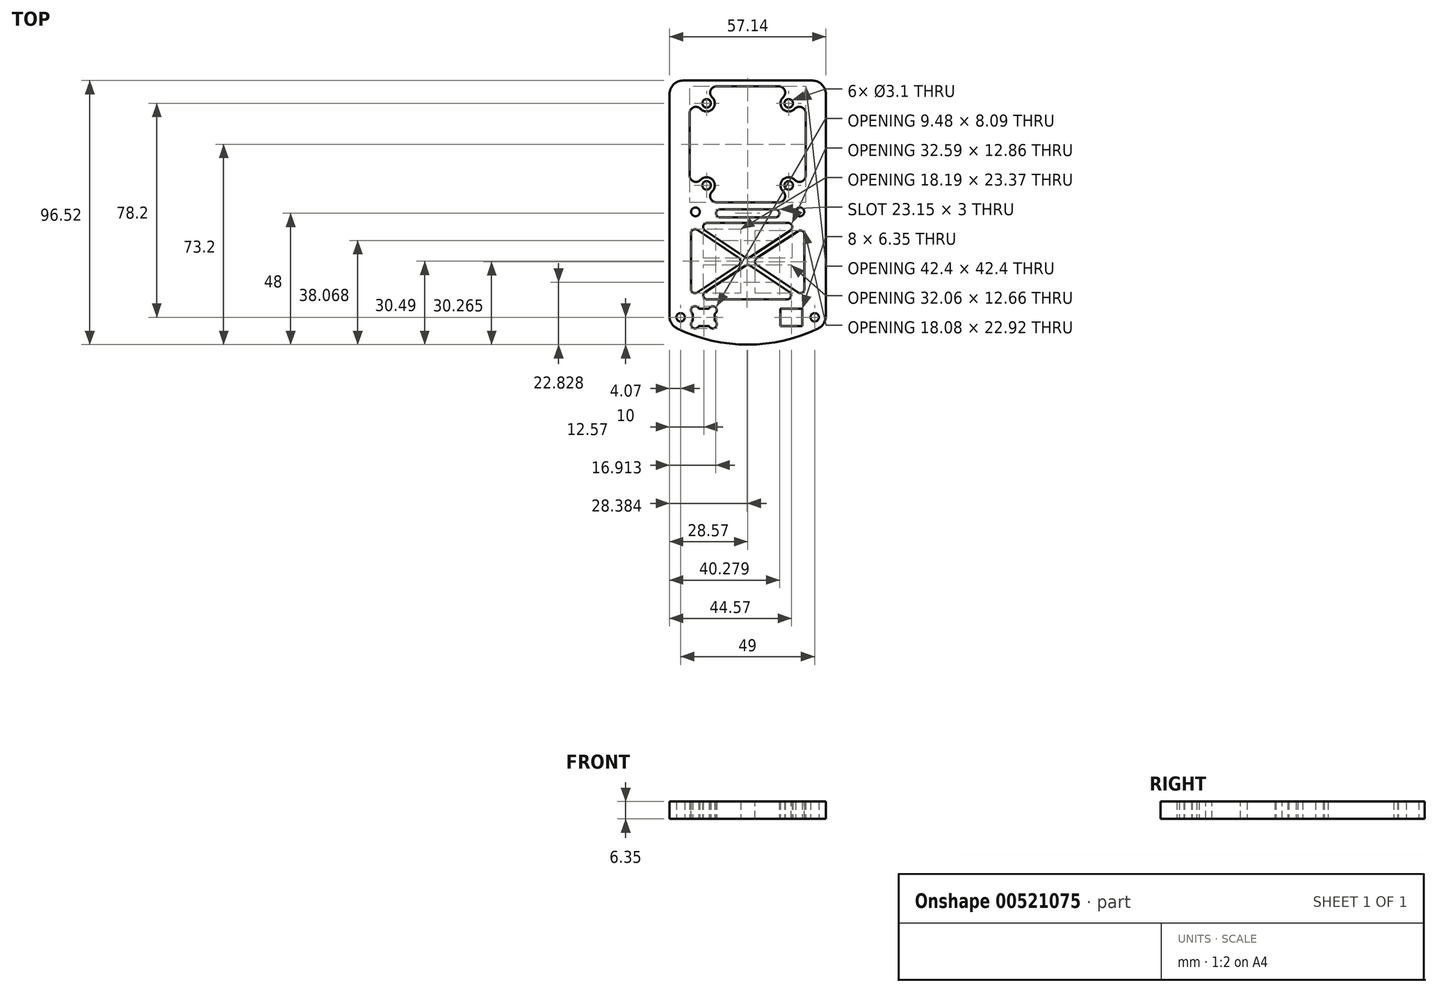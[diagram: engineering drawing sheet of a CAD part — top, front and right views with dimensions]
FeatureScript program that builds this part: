
annotation { "Feature Type Name" : "Feature", "Feature Type Description" : "" }
export const myFeature = defineFeature(function(context is Context, id is Id, definition is map)
    precondition{}
    {
        {
            var Q0;
            Q0=qCreatedBy(makeId("Top.planeOp"),FACE);
            var sketch = newSketch(context, id + "F0", { "sketchPlane" : qUnion([Q0])});
            skLineSegment(sketch, "E0.bottom", {"start": v(23.58, 47.02) * mm, "end": v(-23.58, 47.02) * mm});
            skLineSegment(sketch, "E0.top", {"start": v(23.58, -49.5) * mm, "end": v(-23.58, -49.5) * mm, "construction": true});
            skLineSegment(sketch, "E0.left", {"start": v(28.57, 42.02) * mm, "end": v(28.57, -39.08) * mm});
            skLineSegment(sketch, "E0.right", {"start": v(-28.58, 42.02) * mm, "end": v(-28.58, -39.08) * mm});
            skPoint(sketch, "E0.middle", {"position": v(0, 0) * mm});
            skCircle(sketch, "E1", {"center": v(-24.5, -39.5) * mm, "radius": 1.55 * mm});
            skLineSegment(sketch, "E2", {"start": v(0, 44.9) * mm, "end": v(11.41, 44.9) * mm});
            skLineSegment(sketch, "E3", {"start": v(21.2, 35.11) * mm, "end": v(21.2, 23.7) * mm});
            skLineSegment(sketch, "E4", {"start": v(36.97, 23.7) * mm, "end": v(-37.23, 23.7) * mm, "construction": true});
            skCircle(sketch, "E5", {"center": v(-19.08, -0.98) * mm, "radius": 1.6 * mm});
            skLineSegment(sketch, "E6.MirrorCS", {"start": v(0, 44.9) * mm, "end": v(-11.41, 44.9) * mm});
            skLineSegment(sketch, "E7.MirrorCS", {"start": v(-21.2, 35.11) * mm, "end": v(-21.2, 23.7) * mm});
            skLineSegment(sketch, "E8.MirrorCS", {"start": v(21.2, 12.29) * mm, "end": v(21.2, 23.7) * mm});
            skLineSegment(sketch, "E9.MirrorCS", {"start": v(0, 2.5) * mm, "end": v(11.41, 2.5) * mm});
            skLineSegment(sketch, "E10.MirrorCS", {"start": v(0, 2.5) * mm, "end": v(-11.41, 2.5) * mm});
            skLineSegment(sketch, "E11.MirrorCS", {"start": v(-21.2, 12.29) * mm, "end": v(-21.2, 23.7) * mm});
            skPoint(sketch, "E12.MirrorP", {"position": v(0, 47.4) * mm});
            skPoint(sketch, "E13.visualSharp", {"position": v(-28.58, 47.02) * mm});
            skArc(sketch, "E13.filletArc", {"start": v(-23.58, 47.02) * mm, "mid": v(-27.11, 45.56) * mm, "end": v(-28.58, 42.02) * mm});
            skPoint(sketch, "E14.visualSharp", {"position": v(28.57, 47.02) * mm});
            skArc(sketch, "E14.filletArc", {"start": v(28.58, 42.02) * mm, "mid": v(27.11, 45.56) * mm, "end": v(23.58, 47.02) * mm});
            skCircle(sketch, "E15", {"center": v(-15, 8.7) * mm, "radius": 1.55 * mm});
            skCircle(sketch, "E16.MirrorC", {"center": v(15, 8.7) * mm, "radius": 1.55 * mm});
            skCircle(sketch, "E17.MirrorC", {"center": v(15, 38.7) * mm, "radius": 1.55 * mm});
            skCircle(sketch, "E18.MirrorC", {"center": v(-15, 38.7) * mm, "radius": 1.55 * mm});
            skCircle(sketch, "E19.MirrorC", {"center": v(19.08, -0.98) * mm, "radius": 1.6 * mm});
            skArc(sketch, "E20", {"start": v(10.07, -3) * mm, "mid": v(11.57, -1.5) * mm, "end": v(10.07, 0) * mm});
            skArc(sketch, "E21", {"start": v(-11.41, 2.5) * mm, "mid": v(-13.55, 3.96) * mm, "end": v(-12.97, 6.5) * mm});
            skArc(sketch, "E22", {"start": v(-17.2, 10.73) * mm, "mid": v(-19.74, 10.15) * mm, "end": v(-21.2, 12.29) * mm});
            skArc(sketch, "E23.MirrorCS", {"start": v(11.41, 2.5) * mm, "mid": v(13.55, 3.96) * mm, "end": v(12.97, 6.5) * mm});
            skArc(sketch, "E24.MirrorCS", {"start": v(17.2, 10.73) * mm, "mid": v(19.74, 10.15) * mm, "end": v(21.2, 12.29) * mm});
            skArc(sketch, "E25.MirrorCS", {"start": v(-17.2, 36.67) * mm, "mid": v(-19.74, 37.25) * mm, "end": v(-21.2, 35.11) * mm});
            skArc(sketch, "E26.MirrorCS", {"start": v(-11.41, 44.9) * mm, "mid": v(-13.55, 43.44) * mm, "end": v(-12.97, 40.9) * mm});
            skArc(sketch, "E27.MirrorCS", {"start": v(17.2, 36.67) * mm, "mid": v(19.74, 37.25) * mm, "end": v(21.2, 35.11) * mm});
            skArc(sketch, "E28.MirrorCS", {"start": v(11.41, 44.9) * mm, "mid": v(13.55, 43.44) * mm, "end": v(12.97, 40.9) * mm});
            skLineSegment(sketch, "E29.bottom", {"start": v(10.08, 0) * mm, "end": v(0, 0) * mm});
            skLineSegment(sketch, "E29.top", {"start": v(10.07, -3) * mm, "end": v(0, -3) * mm});
            skLineSegment(sketch, "E29.right", {"start": v(0, 0) * mm, "end": v(0, -3) * mm});
            skLineSegment(sketch, "E30.MirrorCS", {"start": v(-10.07, -3) * mm, "end": v(0, -3) * mm});
            skArc(sketch, "E31.MirrorC", {"start": v(-10.07, -3) * mm, "mid": v(-11.57, -1.5) * mm, "end": v(-10.08, 0) * mm});
            skLineSegment(sketch, "E32.MirrorCS", {"start": v(-10.08, 0) * mm, "end": v(0, 0) * mm});
            skLineSegment(sketch, "E33", {"start": v(10.08, 0) * mm, "end": v(10.08, -3) * mm, "construction": true});
            skLineSegment(sketch, "E34", {"start": v(-10.08, 0) * mm, "end": v(-10.08, -3) * mm, "construction": true});
            skLineSegment(sketch, "E35", {"start": v(0, 23.7) * mm, "end": v(-36.43, -12.73) * mm, "construction": true});
            skPoint(sketch, "E36.orphan", {"position": v(0, 57.71) * mm});
            skArc(sketch, "E37", {"start": v(-12.97, 6.5) * mm, "mid": v(-12.88, 10.82) * mm, "end": v(-17.2, 10.73) * mm});
            skArc(sketch, "E38.MirrorCS", {"start": v(12.97, 6.5) * mm, "mid": v(12.88, 10.82) * mm, "end": v(17.2, 10.73) * mm});
            skArc(sketch, "E39.MirrorCS", {"start": v(-12.97, 40.9) * mm, "mid": v(-12.88, 36.58) * mm, "end": v(-17.2, 36.67) * mm});
            skArc(sketch, "E40.MirrorCS", {"start": v(12.97, 40.9) * mm, "mid": v(12.88, 36.58) * mm, "end": v(17.2, 36.67) * mm});
            skLineSegment(sketch, "E41", {"start": v(-24.5, -39.5) * mm, "end": v(24.5, -39.5) * mm, "construction": true});
            skLineSegment(sketch, "E42.bottom", {"start": v(-12, -36.33) * mm, "end": v(-20, -36.33) * mm});
            skLineSegment(sketch, "E42.top", {"start": v(-12, -42.68) * mm, "end": v(-20, -42.68) * mm});
            skLineSegment(sketch, "E42.left", {"start": v(-12, -36.33) * mm, "end": v(-12, -42.68) * mm});
            skLineSegment(sketch, "E42.right", {"start": v(-20, -36.33) * mm, "end": v(-20, -42.68) * mm});
            skPoint(sketch, "E42.middle", {"position": v(-16, -39.5) * mm});
            skLineSegment(sketch, "E43", {"start": v(0, 67.13) * mm, "end": v(0, -67.36) * mm, "construction": true});
            skPoint(sketch, "E43.endSnap0", {"position": v(0, -49.5) * mm});
            skLineSegment(sketch, "E44.MirrorCS", {"start": v(12, -36.33) * mm, "end": v(12, -42.68) * mm});
            skLineSegment(sketch, "E45.MirrorCS", {"start": v(12, -42.68) * mm, "end": v(20, -42.68) * mm});
            skLineSegment(sketch, "E46.MirrorCS", {"start": v(20, -36.33) * mm, "end": v(20, -42.68) * mm});
            skLineSegment(sketch, "E47.MirrorCS", {"start": v(12, -36.33) * mm, "end": v(20, -36.33) * mm});
            skCircle(sketch, "E48.MirrorC", {"center": v(24.5, -39.5) * mm, "radius": 1.55 * mm});
            skArc(sketch, "E49", {"start": v(-28.58, -39.08) * mm, "mid": v(-27.81, -41.74) * mm, "end": v(-25.76, -43.58) * mm});
            skArc(sketch, "E50", {"start": v(28.58, -39.08) * mm, "mid": v(27.81, -41.74) * mm, "end": v(25.76, -43.58) * mm});
            skArc(sketch, "E51", {"start": v(-25.76, -43.58) * mm, "mid": v(0, -49.5) * mm, "end": v(25.76, -43.58) * mm});
            skSolve(sketch);
        }
        {
            var Q0;
            Q0 = qSketchRegion(id + "F0", true);
            extrude(context, id + "F1", {"entities" : qUnion([Q0]), "depth" : 6.35 * mm, "offsetDistance" : 25 * mm});
        }
        {
            var Q0;
            Q0=makeQuery(id+"F1.opExtrude","CAP_FACE",FACE,{"disambiguationData":[OSD([sQuery(id+"F0.wireOp",EDGE,"E0.bottom"),sQuery(id+"F0.wireOp",EDGE,"E0.left"),sQuery(id+"F0.wireOp",EDGE,"E0.right"),sQuery(id+"F0.wireOp",EDGE,"E1"),sQuery(id+"F0.wireOp",EDGE,"E3"),sQuery(id+"F0.wireOp",EDGE,"E5"),sQuery(id+"F0.wireOp",EDGE,"E7.MirrorCS"),sQuery(id+"F0.wireOp",EDGE,"E8.MirrorCS"),sQuery(id+"F0.wireOp",EDGE,"E9.MirrorCS"),sQuery(id+"F0.wireOp",EDGE,"E10.MirrorCS"),sQuery(id+"F0.wireOp",EDGE,"E11.MirrorCS"),sQuery(id+"F0.wireOp",EDGE,"E13.filletArc"),sQuery(id+"F0.wireOp",EDGE,"E14.filletArc"),sQuery(id+"F0.wireOp",EDGE,"E16.MirrorC"),sQuery(id+"F0.wireOp",EDGE,"E15"),sQuery(id+"F0.wireOp",EDGE,"E17.MirrorC"),sQuery(id+"F0.wireOp",EDGE,"E18.MirrorC"),sQuery(id+"F0.wireOp",EDGE,"E19.MirrorC"),sQuery(id+"F0.wireOp",EDGE,"E20"),sQuery(id+"F0.wireOp",EDGE,"E21"),sQuery(id+"F0.wireOp",EDGE,"E22"),sQuery(id+"F0.wireOp",EDGE,"E23.MirrorCS"),sQuery(id+"F0.wireOp",EDGE,"E24.MirrorCS"),sQuery(id+"F0.wireOp",EDGE,"E2"),sQuery(id+"F0.wireOp",EDGE,"E6.MirrorCS"),sQuery(id+"F0.wireOp",EDGE,"E25.MirrorCS"),sQuery(id+"F0.wireOp",EDGE,"E26.MirrorCS"),sQuery(id+"F0.wireOp",EDGE,"E27.MirrorCS"),sQuery(id+"F0.wireOp",EDGE,"E28.MirrorCS"),sQuery(id+"F0.wireOp",EDGE,"E29.right"),sQuery(id+"F0.wireOp",EDGE,"E30.MirrorCS"),sQuery(id+"F0.wireOp",EDGE,"E31.MirrorC"),sQuery(id+"F0.wireOp",EDGE,"E32.MirrorCS"),sQuery(id+"F0.wireOp",EDGE,"E37"),sQuery(id+"F0.wireOp",EDGE,"E38.MirrorCS"),sQuery(id+"F0.wireOp",EDGE,"E39.MirrorCS"),sQuery(id+"F0.wireOp",EDGE,"E40.MirrorCS"),sQuery(id+"F0.wireOp",EDGE,"E42.bottom"),sQuery(id+"F0.wireOp",EDGE,"E42.top"),sQuery(id+"F0.wireOp",EDGE,"E42.left"),sQuery(id+"F0.wireOp",EDGE,"E42.right"),sQuery(id+"F0.wireOp",EDGE,"E44.MirrorCS"),sQuery(id+"F0.wireOp",EDGE,"E45.MirrorCS"),sQuery(id+"F0.wireOp",EDGE,"E46.MirrorCS"),sQuery(id+"F0.wireOp",EDGE,"E47.MirrorCS"),sQuery(id+"F0.wireOp",EDGE,"E48.MirrorC"),sQuery(id+"F0.wireOp",EDGE,"E49"),sQuery(id+"F0.wireOp",EDGE,"E50"),sQuery(id+"F0.wireOp",EDGE,"E51")])],"isStart":false});
            var sketch = newSketch(context, id + "F2", { "sketchPlane" : qUnion([Q0])});
            skLineSegment(sketch, "E52.bottom", {"start": v(20.75, -5) * mm, "end": v(-20.75, -5) * mm});
            skLineSegment(sketch, "E52.top", {"start": v(20.75, -33) * mm, "end": v(-20.75, -33) * mm});
            skLineSegment(sketch, "E52.left", {"start": v(20.75, -5) * mm, "end": v(20.75, -33) * mm});
            skLineSegment(sketch, "E52.right", {"start": v(-20.75, -5) * mm, "end": v(-20.75, -33) * mm});
            skPoint(sketch, "E52.middle", {"position": v(0, -19) * mm});
            skLineSegment(sketch, "E53", {"start": v(-19.75, -5) * mm, "end": v(19.75, -5) * mm, "construction": true});
            skLineSegment(sketch, "E54", {"start": v(20.75, -6.5) * mm, "end": v(20.75, -32) * mm, "construction": true});
            skLineSegment(sketch, "E55", {"start": v(19.25, -33) * mm, "end": v(-19.75, -33) * mm, "construction": true});
            skLineSegment(sketch, "E56", {"start": v(-20.75, -6) * mm, "end": v(-20.75, -32) * mm, "construction": true});
            skLineSegment(sketch, "E57", {"start": v(-19.75, -5) * mm, "end": v(20.75, -32) * mm});
            skLineSegment(sketch, "E58", {"start": v(19.25, -33) * mm, "end": v(-20.75, -6) * mm});
            skLineSegment(sketch, "E59", {"start": v(-20.75, -32) * mm, "end": v(19.75, -5) * mm});
            skLineSegment(sketch, "E60", {"start": v(-19.75, -33) * mm, "end": v(20.75, -6.5) * mm});
            skSolve(sketch);
        }
        {
            var Q0;
            {var subQ0=sQuery(id+"F2.wireOp",EDGE,"E58");var subQ1=sQuery(id+"F2.wireOp",EDGE,"E52.right");var subQ2=makeQuery(id+"F2.imprint","INTERSECT",VERTEX,{"derivedFrom":[subQ1,subQ0]});Q0=makeQuery(id+"F2.imprint","IMPRINT",FACE,{"disambiguationData":[TD([[makeQuery(id+"F2.imprint","IMPRINT",EDGE,{"disambiguationData":[TD([[subQ2,-1.0]])],"derivedFrom":subQ1}),1.0]])]});}
            var Q1;
            {var subQ0=sQuery(id+"F2.wireOp",EDGE,"E57");var subQ1=sQuery(id+"F2.wireOp",EDGE,"E52.bottom");var subQ2=makeQuery(id+"F2.imprint","INTERSECT",VERTEX,{"derivedFrom":[subQ1,subQ0]});Q1=makeQuery(id+"F2.imprint","IMPRINT",FACE,{"disambiguationData":[TD([[makeQuery(id+"F2.imprint","IMPRINT",EDGE,{"disambiguationData":[TD([[subQ2,1.0]])],"derivedFrom":subQ1}),1.0]])]});}
            var Q2;
            {var subQ0=sQuery(id+"F2.wireOp",EDGE,"E57");var subQ1=sQuery(id+"F2.wireOp",EDGE,"E52.left");var subQ2=makeQuery(id+"F2.imprint","INTERSECT",VERTEX,{"derivedFrom":[subQ1,subQ0]});Q2=makeQuery(id+"F2.imprint","IMPRINT",FACE,{"disambiguationData":[TD([[makeQuery(id+"F2.imprint","IMPRINT",EDGE,{"disambiguationData":[TD([[subQ2,1.0]])],"derivedFrom":subQ1}),-1.0]])]});}
            var Q3;
            {var subQ0=sQuery(id+"F2.wireOp",EDGE,"E58");var subQ1=sQuery(id+"F2.wireOp",EDGE,"E52.top");var subQ2=makeQuery(id+"F2.imprint","INTERSECT",VERTEX,{"derivedFrom":[subQ1,subQ0]});Q3=makeQuery(id+"F2.imprint","IMPRINT",FACE,{"disambiguationData":[TD([[makeQuery(id+"F2.imprint","IMPRINT",EDGE,{"disambiguationData":[TD([[subQ2,-1.0]])],"derivedFrom":subQ1}),-1.0]])]});}
            extrude(context, id + "F3", {"entities" : qUnion([Q0, Q1, Q2, Q3]), "operationType" : NewBodyOperationType.REMOVE, "oppositeDirection" : true, "depth" : 25 * mm, "offsetDistance" : 25 * mm});
        }
        {
            var Q0;
            Q0=makeQuery(id+"F3.boolean.opBoolean","COPY",EDGE,{"derivedFrom":makeQuery(id+"F3.opExtrude","SWEPT_EDGE",EDGE,{"disambiguationData":[OSD([sQuery(id+"F2.wireOp",EDGE,"E52.right"),sQuery(id+"F2.wireOp",EDGE,"E58")])]})});
            var Q1;
            Q1=makeQuery(id+"F3.boolean.opBoolean","COPY",EDGE,{"derivedFrom":makeQuery(id+"F3.opExtrude","SWEPT_EDGE",EDGE,{"disambiguationData":[OSD([sQuery(id+"F2.wireOp",EDGE,"E52.right"),sQuery(id+"F2.wireOp",EDGE,"E59")])]})});
            var Q2;
            Q2=makeQuery(id+"F3.boolean.opBoolean","COPY",EDGE,{"derivedFrom":makeQuery(id+"F3.opExtrude","SWEPT_EDGE",EDGE,{"disambiguationData":[OSD([sQuery(id+"F2.wireOp",EDGE,"E52.bottom"),sQuery(id+"F2.wireOp",EDGE,"E57")])]})});
            var Q3;
            Q3=makeQuery(id+"F3.boolean.opBoolean","COPY",EDGE,{"derivedFrom":makeQuery(id+"F3.opExtrude","SWEPT_EDGE",EDGE,{"disambiguationData":[OSD([sQuery(id+"F2.wireOp",EDGE,"E52.bottom"),sQuery(id+"F2.wireOp",EDGE,"E59")])]})});
            var Q4;
            Q4=makeQuery(id+"F3.boolean.opBoolean","COPY",EDGE,{"derivedFrom":makeQuery(id+"F3.opExtrude","SWEPT_EDGE",EDGE,{"disambiguationData":[OSD([sQuery(id+"F2.wireOp",EDGE,"E52.left"),sQuery(id+"F2.wireOp",EDGE,"E60")])]})});
            var Q5;
            Q5=makeQuery(id+"F3.boolean.opBoolean","COPY",EDGE,{"derivedFrom":makeQuery(id+"F3.opExtrude","SWEPT_EDGE",EDGE,{"disambiguationData":[OSD([sQuery(id+"F2.wireOp",EDGE,"E52.left"),sQuery(id+"F2.wireOp",EDGE,"E57")])]})});
            var Q6;
            Q6=makeQuery(id+"F3.boolean.opBoolean","COPY",EDGE,{"derivedFrom":makeQuery(id+"F3.opExtrude","SWEPT_EDGE",EDGE,{"disambiguationData":[OSD([sQuery(id+"F2.wireOp",EDGE,"E52.top"),sQuery(id+"F2.wireOp",EDGE,"E58")])]})});
            var Q7;
            Q7=makeQuery(id+"F3.boolean.opBoolean","COPY",EDGE,{"derivedFrom":makeQuery(id+"F3.opExtrude","SWEPT_EDGE",EDGE,{"disambiguationData":[OSD([sQuery(id+"F2.wireOp",EDGE,"E52.top"),sQuery(id+"F2.wireOp",EDGE,"E60")])]})});
            var Q8;
            Q8=makeQuery(id+"F3.boolean.opBoolean","COPY",EDGE,{"derivedFrom":makeQuery(id+"F3.opExtrude","SWEPT_EDGE",EDGE,{"disambiguationData":[OSD([sQuery(id+"F2.wireOp",EDGE,"E58"),sQuery(id+"F2.wireOp",EDGE,"E60")])]})});
            var Q9;
            Q9=makeQuery(id+"F3.boolean.opBoolean","COPY",EDGE,{"derivedFrom":makeQuery(id+"F3.opExtrude","SWEPT_EDGE",EDGE,{"disambiguationData":[OSD([sQuery(id+"F2.wireOp",EDGE,"E57"),sQuery(id+"F2.wireOp",EDGE,"E60")])]})});
            var Q10;
            Q10=makeQuery(id+"F3.boolean.opBoolean","COPY",EDGE,{"derivedFrom":makeQuery(id+"F3.opExtrude","SWEPT_EDGE",EDGE,{"disambiguationData":[OSD([sQuery(id+"F2.wireOp",EDGE,"E57"),sQuery(id+"F2.wireOp",EDGE,"E59")])]})});
            var Q11;
            Q11=makeQuery(id+"F3.boolean.opBoolean","COPY",EDGE,{"derivedFrom":makeQuery(id+"F3.opExtrude","SWEPT_EDGE",EDGE,{"disambiguationData":[OSD([sQuery(id+"F2.wireOp",EDGE,"E58"),sQuery(id+"F2.wireOp",EDGE,"E59")])]})});
            fillet(context, id + "F4", {"entities" : qUnion([Q0, Q1, Q2, Q3, Q4, Q5, Q6, Q7, Q8, Q9, Q10, Q11]), "radius" : 1.5 * mm, "tangentPropagation" : true, "allowEdgeOverflow" : false});
        }
        {
            var Q0;
            Q0=makeQuery(id+"F1.opExtrude","CAP_FACE",FACE,{"disambiguationData":[OSD([sQuery(id+"F0.wireOp",EDGE,"E0.bottom"),sQuery(id+"F0.wireOp",EDGE,"E0.left"),sQuery(id+"F0.wireOp",EDGE,"E0.right"),sQuery(id+"F0.wireOp",EDGE,"E1"),sQuery(id+"F0.wireOp",EDGE,"E3"),sQuery(id+"F0.wireOp",EDGE,"E5"),sQuery(id+"F0.wireOp",EDGE,"E7.MirrorCS"),sQuery(id+"F0.wireOp",EDGE,"E8.MirrorCS"),sQuery(id+"F0.wireOp",EDGE,"E9.MirrorCS"),sQuery(id+"F0.wireOp",EDGE,"E10.MirrorCS"),sQuery(id+"F0.wireOp",EDGE,"E11.MirrorCS"),sQuery(id+"F0.wireOp",EDGE,"E13.filletArc"),sQuery(id+"F0.wireOp",EDGE,"E14.filletArc"),sQuery(id+"F0.wireOp",EDGE,"E16.MirrorC"),sQuery(id+"F0.wireOp",EDGE,"E15"),sQuery(id+"F0.wireOp",EDGE,"E17.MirrorC"),sQuery(id+"F0.wireOp",EDGE,"E18.MirrorC"),sQuery(id+"F0.wireOp",EDGE,"E19.MirrorC"),sQuery(id+"F0.wireOp",EDGE,"E20"),sQuery(id+"F0.wireOp",EDGE,"E21"),sQuery(id+"F0.wireOp",EDGE,"E22"),sQuery(id+"F0.wireOp",EDGE,"E23.MirrorCS"),sQuery(id+"F0.wireOp",EDGE,"E24.MirrorCS"),sQuery(id+"F0.wireOp",EDGE,"E2"),sQuery(id+"F0.wireOp",EDGE,"E6.MirrorCS"),sQuery(id+"F0.wireOp",EDGE,"E25.MirrorCS"),sQuery(id+"F0.wireOp",EDGE,"E26.MirrorCS"),sQuery(id+"F0.wireOp",EDGE,"E27.MirrorCS"),sQuery(id+"F0.wireOp",EDGE,"E28.MirrorCS"),sQuery(id+"F0.wireOp",EDGE,"E29.bottom"),sQuery(id+"F0.wireOp",EDGE,"E29.top"),sQuery(id+"F0.wireOp",EDGE,"E30.MirrorCS"),sQuery(id+"F0.wireOp",EDGE,"E31.MirrorC"),sQuery(id+"F0.wireOp",EDGE,"E32.MirrorCS"),sQuery(id+"F0.wireOp",EDGE,"E37"),sQuery(id+"F0.wireOp",EDGE,"E38.MirrorCS"),sQuery(id+"F0.wireOp",EDGE,"E39.MirrorCS"),sQuery(id+"F0.wireOp",EDGE,"E40.MirrorCS"),sQuery(id+"F0.wireOp",EDGE,"E42.bottom"),sQuery(id+"F0.wireOp",EDGE,"E42.top"),sQuery(id+"F0.wireOp",EDGE,"E42.left"),sQuery(id+"F0.wireOp",EDGE,"E42.right"),sQuery(id+"F0.wireOp",EDGE,"E44.MirrorCS"),sQuery(id+"F0.wireOp",EDGE,"E45.MirrorCS"),sQuery(id+"F0.wireOp",EDGE,"E46.MirrorCS"),sQuery(id+"F0.wireOp",EDGE,"E47.MirrorCS"),sQuery(id+"F0.wireOp",EDGE,"E48.MirrorC"),sQuery(id+"F0.wireOp",EDGE,"E49"),sQuery(id+"F0.wireOp",EDGE,"E50"),sQuery(id+"F0.wireOp",EDGE,"E51")])],"isStart":true});
            var sketch = newSketch(context, id + "F5", { "sketchPlane" : qUnion([Q0])});
            skLineSegment(sketch, "E61", {"start": v(-12, 36.33) * mm, "end": v(-20, 42.68) * mm, "construction": true});
            skLineSegment(sketch, "E62", {"start": v(-12, 42.68) * mm, "end": v(-20, 36.33) * mm, "construction": true});
            skLineSegment(sketch, "E63.bottom", {"start": v(-19.25, 36.92) * mm, "end": v(-12.75, 36.92) * mm, "construction": true});
            skLineSegment(sketch, "E63.top", {"start": v(-19.25, 42.08) * mm, "end": v(-12.75, 42.08) * mm, "construction": true});
            skLineSegment(sketch, "E63.left", {"start": v(-19.25, 36.92) * mm, "end": v(-19.25, 42.08) * mm, "construction": true});
            skLineSegment(sketch, "E63.right", {"start": v(-12.75, 36.92) * mm, "end": v(-12.75, 42.08) * mm, "construction": true});
            skPoint(sketch, "E63.middle", {"position": v(-16, 39.5) * mm});
            skCircle(sketch, "E64", {"center": v(-19.25, 36.92) * mm, "radius": 1.5 * mm});
            skCircle(sketch, "E65", {"center": v(-19.25, 42.08) * mm, "radius": 1.5 * mm});
            skCircle(sketch, "E66", {"center": v(-12.75, 42.08) * mm, "radius": 1.5 * mm});
            skCircle(sketch, "E67", {"center": v(-12.75, 36.92) * mm, "radius": 1.5 * mm});
            skLineSegment(sketch, "E68", {"start": v(0, 25.02) * mm, "end": v(0, 58.55) * mm, "construction": true});
            skCircle(sketch, "E69.MirrorC", {"center": v(12.75, 36.92) * mm, "radius": 1.5 * mm});
            skCircle(sketch, "E70.MirrorC", {"center": v(12.75, 42.08) * mm, "radius": 1.5 * mm});
            skCircle(sketch, "E71.MirrorC", {"center": v(19.25, 42.08) * mm, "radius": 1.5 * mm});
            skCircle(sketch, "E72.MirrorC", {"center": v(19.25, 36.92) * mm, "radius": 1.5 * mm});
            skSolve(sketch);
        }
        {
            var Q0;
            {var subQ0=sQuery(id+"F5.wireOp",EDGE,"E67");var subQ1=makeQuery(id+"F1.opExtrude","CAP_EDGE",EDGE,{"disambiguationData":[OSD([sQuery(id+"F0.wireOp",EDGE,"E42.bottom")])],"isStart":true});var subQ2=makeQuery(id+"F5.imprint","INTERSECT",VERTEX,{"derivedFrom":[subQ1,subQ0]});Q0=makeQuery(id+"F5.imprint","IMPRINT",FACE,{"disambiguationData":[TD([[makeQuery(id+"F5.imprint","IMPRINT",EDGE,{"disambiguationData":[TD([[subQ2,-1.0]])],"derivedFrom":subQ0}),1.0]])]});}
            var Q1;
            {var subQ0=sQuery(id+"F5.wireOp",EDGE,"E66");var subQ1=makeQuery(id+"F1.opExtrude","CAP_EDGE",EDGE,{"disambiguationData":[OSD([sQuery(id+"F0.wireOp",EDGE,"E42.top")])],"isStart":true});var subQ2=makeQuery(id+"F5.imprint","INTERSECT",VERTEX,{"derivedFrom":[subQ1,subQ0]});Q1=makeQuery(id+"F5.imprint","IMPRINT",FACE,{"disambiguationData":[TD([[makeQuery(id+"F5.imprint","IMPRINT",EDGE,{"disambiguationData":[TD([[subQ2,1.0]])],"derivedFrom":subQ0}),1.0]])]});}
            var Q2;
            {var subQ0=sQuery(id+"F5.wireOp",EDGE,"E65");var subQ1=makeQuery(id+"F1.opExtrude","CAP_EDGE",EDGE,{"disambiguationData":[OSD([sQuery(id+"F0.wireOp",EDGE,"E42.top")])],"isStart":true});var subQ2=makeQuery(id+"F5.imprint","INTERSECT",VERTEX,{"derivedFrom":[subQ1,subQ0]});Q2=makeQuery(id+"F5.imprint","IMPRINT",FACE,{"disambiguationData":[TD([[makeQuery(id+"F5.imprint","IMPRINT",EDGE,{"disambiguationData":[TD([[subQ2,-1.0]])],"derivedFrom":subQ0}),1.0]])]});}
            var Q3;
            {var subQ0=sQuery(id+"F5.wireOp",EDGE,"E64");var subQ1=makeQuery(id+"F1.opExtrude","CAP_EDGE",EDGE,{"disambiguationData":[OSD([sQuery(id+"F0.wireOp",EDGE,"E42.bottom")])],"isStart":true});var subQ2=makeQuery(id+"F5.imprint","INTERSECT",VERTEX,{"derivedFrom":[subQ1,subQ0]});Q3=makeQuery(id+"F5.imprint","IMPRINT",FACE,{"disambiguationData":[TD([[makeQuery(id+"F5.imprint","IMPRINT",EDGE,{"disambiguationData":[TD([[subQ2,1.0]])],"derivedFrom":subQ0}),1.0]])]});}
            var Q4;
            {var subQ0=sQuery(id+"F5.wireOp",EDGE,"E69.MirrorC");var subQ1=makeQuery(id+"F1.opExtrude","CAP_EDGE",EDGE,{"disambiguationData":[OSD([sQuery(id+"F0.wireOp",EDGE,"E44.MirrorCS")])],"isStart":true});var subQ2=makeQuery(id+"F5.imprint","INTERSECT",VERTEX,{"derivedFrom":[subQ1,subQ0]});Q4=makeQuery(id+"F5.imprint","IMPRINT",FACE,{"disambiguationData":[TD([[makeQuery(id+"F5.imprint","IMPRINT",EDGE,{"disambiguationData":[TD([[subQ2,1.0]])],"derivedFrom":subQ0}),-1.0]])]});}
            var Q5;
            {var subQ0=sQuery(id+"F5.wireOp",EDGE,"E70.MirrorC");var subQ1=makeQuery(id+"F1.opExtrude","CAP_EDGE",EDGE,{"disambiguationData":[OSD([sQuery(id+"F0.wireOp",EDGE,"E44.MirrorCS")])],"isStart":true});var subQ2=makeQuery(id+"F5.imprint","INTERSECT",VERTEX,{"derivedFrom":[subQ1,subQ0]});Q5=makeQuery(id+"F5.imprint","IMPRINT",FACE,{"disambiguationData":[TD([[makeQuery(id+"F5.imprint","IMPRINT",EDGE,{"disambiguationData":[TD([[subQ2,-1.0]])],"derivedFrom":subQ0}),-1.0]])]});}
            var Q6;
            {var subQ0=sQuery(id+"F5.wireOp",EDGE,"E71.MirrorC");var subQ1=makeQuery(id+"F1.opExtrude","CAP_EDGE",EDGE,{"disambiguationData":[OSD([sQuery(id+"F0.wireOp",EDGE,"E45.MirrorCS")])],"isStart":true});var subQ2=makeQuery(id+"F5.imprint","INTERSECT",VERTEX,{"derivedFrom":[subQ1,subQ0]});Q6=makeQuery(id+"F5.imprint","IMPRINT",FACE,{"disambiguationData":[TD([[makeQuery(id+"F5.imprint","IMPRINT",EDGE,{"disambiguationData":[TD([[subQ2,-1.0]])],"derivedFrom":subQ0}),-1.0]])]});}
            var Q7;
            {var subQ0=sQuery(id+"F5.wireOp",EDGE,"E72.MirrorC");var subQ1=makeQuery(id+"F1.opExtrude","CAP_EDGE",EDGE,{"disambiguationData":[OSD([sQuery(id+"F0.wireOp",EDGE,"E46.MirrorCS")])],"isStart":true});var subQ2=makeQuery(id+"F5.imprint","INTERSECT",VERTEX,{"derivedFrom":[subQ1,subQ0]});Q7=makeQuery(id+"F5.imprint","IMPRINT",FACE,{"disambiguationData":[TD([[makeQuery(id+"F5.imprint","IMPRINT",EDGE,{"disambiguationData":[TD([[subQ2,-1.0]])],"derivedFrom":subQ0}),-1.0]])]});}
            extrude(context, id + "F6", {"entities" : qUnion([Q0, Q1, Q2, Q3, Q4, Q5, Q6, Q7]), "operationType" : NewBodyOperationType.REMOVE, "oppositeDirection" : true, "depth" : 25 * mm, "offsetDistance" : 25 * mm});
        }
    });
